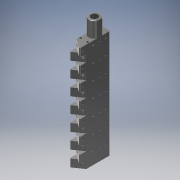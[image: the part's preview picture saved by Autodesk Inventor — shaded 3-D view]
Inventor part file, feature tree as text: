
AUTODESK INVENTOR PART (.ipt)
format: ipt  version: 2018 (Build 220112000, 112)  size: 594,944 bytes
history: native  units: mm
features: hole x12, extrude x9, sketch x7, other x6, plane x4, mirror x2, thread x2, reference x2, pattern_linear x1, fillet x1, revolve x1
ambient origin geometry x8: Origin, YZ Plane, XZ Plane, XY Plane, X Axis, Y Axis, Z Axis, Center Point
bodies: Volumenkörper1 (feature_tree)
feature tree (47):
  extrude  "Extrusion1"  Depth=40.0mm
  hole  "Bohrung1"  [1 undecoded]
  hole  "Bohrung2"  [1 undecoded]
  hole  "Bohrung3"  [1 undecoded]
  hole  "Bohrung4"  [1 undecoded]
  extrude  "Extrusion2"  Depth=10.0mm
  hole  "Bohrung5"  [1 undecoded]
  hole  "Bohrung6"  [1 undecoded]
  plane  "Arbeitsebene1"
  extrude  "Extrusion3"  Depth=10.0mm
  hole  "Bohrung7"  [1 undecoded]
  hole  "Bohrung8"  [1 undecoded]
  plane  "Arbeitsebene2"
  extrude  "Extrusion4"  Depth=10.0mm
  hole  "Bohrung9"  [1 undecoded]
  hole  "Bohrung10"  [1 undecoded]
  pattern_linear  "Rechteckige Anordnung3"  Spacing1=5.0mm  [1 undecoded]
  hole  "Bohrung11"  [1 undecoded]
  plane  "Arbeitsebene3"
  extrude  "Extrusion6"  Depth=10.0mm
  fillet  "Rundung1"  [1 undecoded]
  hole  "Bohrung13"  [1 undecoded]
  extrude  "Extrusion7"  Depth=10.0mm
  mirror  "Spiegeln1"
  extrude  "Extrusion8"  Depth=10.0mm TaperAngle=0.0deg
  revolve  "Umdrehung2"
  extrude  "Extrusion9"  [1 undecoded]
  thread  "Gewinde1"  [1 undecoded]
  plane  "Arbeitsebene4"
  mirror  "Spiegeln2"
  sketch  "Skizze25"  dims[d18=15.0mm d19=2.459mm d20=4.0mm d21=4.0mm d22=2.0mm d23=90.0deg d24=5.0mm d25=20.594885mm d26=8.5mm d27=1.2mm d28=4.0mm d29=4.0mm d30=2.0mm d31=90.0deg d32=5.0mm d33=20.594885mm d35=8.5mm d36=15.0mm d37=1.2mm d38=4.0mm d39=4.0mm d40=2.0mm d41=90.0deg d42=5.0mm d43=20.594885mm d44=8.0mm d45=6.5mm d46=5.5mm d48=0.6mm d49=105.0mm d50=0.0mm d57=8.0mm d58=5.0mm d59=1.8mm d60=6.0mm d61=4.0mm d62=2.0mm d63=90.0deg d64=2.0mm d65=20.594885mm d66=8.0mm d67=15.0mm d68=1.8mm d69=6.0mm d70=4.0mm d71=2.0mm d72=90.0deg d73=2.0mm d74=20.594885mm d75=-5.0mm d76=1.8mm d77=6.108652mm d78=10.0mm d79=0.0mm d80=1.8mm d81=6.0mm d82=4.0mm d83=2.0mm d84=90.0deg d85=14.3mm d86=20.594885mm d87=4.134mm d88=3.0mm d89=4.0mm d90=2.0mm d91=90.0deg d92=4.0mm d93=20.594885mm d94=-15.0mm d95=6.108652mm d96=10.0mm d97=0.0mm d98=1.8mm d99=3.0mm d100=4.0mm d101=2.0mm d102=90.0deg d103=14.3mm d104=20.594885mm d105=4.134mm d106=3.0mm d107=4.0mm d108=2.0mm d109=90.0deg d110=4.0mm d111=20.594885mm d112=50.0mm d114=20.0mm d115=8.566mm d116=3.0mm d117=4.0mm d118=2.0mm d119=90.0deg d120=10.0mm d121=20.594885mm d122=90.0deg d137=15.0mm d138=20.0mm d139=0.0mm d140=1.0mm d141=2.459mm d142=6.0mm d143=4.0mm d144=2.0mm d145=90.0deg d146=8.0mm d147=20.594885mm d155=10.0mm d156=0.0mm d157=10.0mm d158=0.0mm d159=67.5deg d160=4.0mm d161=2.1mm d162=90.0deg d163=8.0mm d164=12.0mm d165=0.0mm d169=8.0mm d170=0.0mm d171=-70.0mm d173=8.8mm d174=8.0mm d175=0.0mm d176=10.0mm d177=0.0mm]
  other  "Fläche verschieben1"
  extrude  "Extrusion10"  Depth=10.0mm TaperAngle=0.0deg
  thread  "Gewinde2"  [1 undecoded]
  sketch  "Skizze4"  dims[d0=13.0mm d1=40.0mm]
  sketch  "Skizze6"  dims[d2=120.0mm d3=0.0mm d4=29.5mm]
  other  "Arbeitsachse1"
  sketch  "Skizze18"  dims[d5=5.25mm d6=5.0mm]
  reference  "Referenz1"
  reference  "Referenz2"
  sketch  "Skizze21"  dims[d7=5.0mm]
  sketch  "Skizze22"  dims[d8=2.459mm d9=4.0mm d10=4.0mm d11=2.0mm d12=90.0deg d13=5.0mm d14=20.594885mm d15=5.25mm]
  sketch  "Skizze23"  dims[d16=29.5mm d17=15.0mm]
  other  "Schnittkanten projizieren1"
  other  "Schnittkanten projizieren2"
  other  "Schnittkanten projizieren3"
  other  "Schnittkanten projizieren5"
note: 17 required parameter values undecoded (feature->parameter linkage not recoverable at this tier; creation-order binding heuristic only, values carry confidence <= 0.55)
